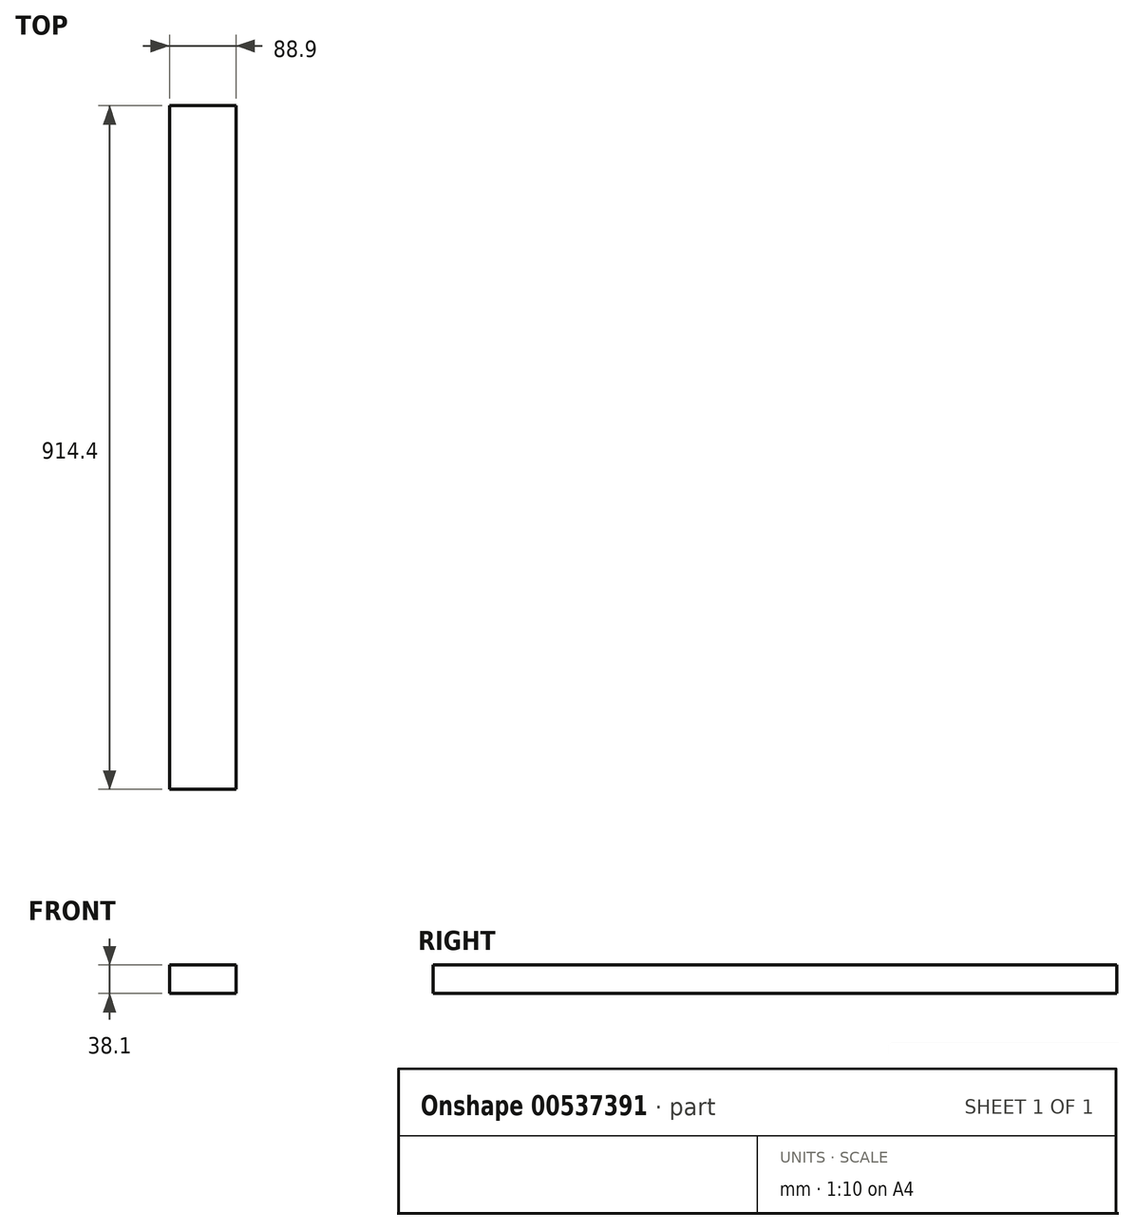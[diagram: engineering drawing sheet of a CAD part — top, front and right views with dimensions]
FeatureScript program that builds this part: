
annotation { "Feature Type Name" : "Feature", "Feature Type Description" : "" }
export const myFeature = defineFeature(function(context is Context, id is Id, definition is map)
    precondition{}
    {
        {
            var Q0;
            Q0=qCreatedBy(makeId("Front.planeOp"),FACE);
            var sketch = newSketch(context, id + "F0", { "sketchPlane" : qUnion([Q0])});
            skLineSegment(sketch, "E0.bottom", {"start": v(44.45, 19.05) * mm, "end": v(-44.45, 19.05) * mm});
            skLineSegment(sketch, "E0.top", {"start": v(44.45, -19.05) * mm, "end": v(-44.45, -19.05) * mm});
            skLineSegment(sketch, "E0.left", {"start": v(44.45, 19.05) * mm, "end": v(44.45, -19.05) * mm});
            skLineSegment(sketch, "E0.right", {"start": v(-44.45, 19.05) * mm, "end": v(-44.45, -19.05) * mm});
            skPoint(sketch, "E0.middle", {"position": v(0, 0) * mm});
            skSolve(sketch);
        }
        {
            var Q0;
            Q0=makeQuery(id+"F0.imprint","IMPRINT",FACE,{"disambiguationData":[TD([[makeQuery(id+"F0.imprint","IMPRINT",EDGE,{"derivedFrom":sQuery(id+"F0.wireOp",EDGE,"E0.bottom")}),1.0]])]});
            extrude(context, id + "F1", {"entities" : qUnion([Q0]), "endBound" : BoundingType.SYMMETRIC, "depth" : 914.4 * mm, "offsetDistance" : 25 * mm});
        }
    });
